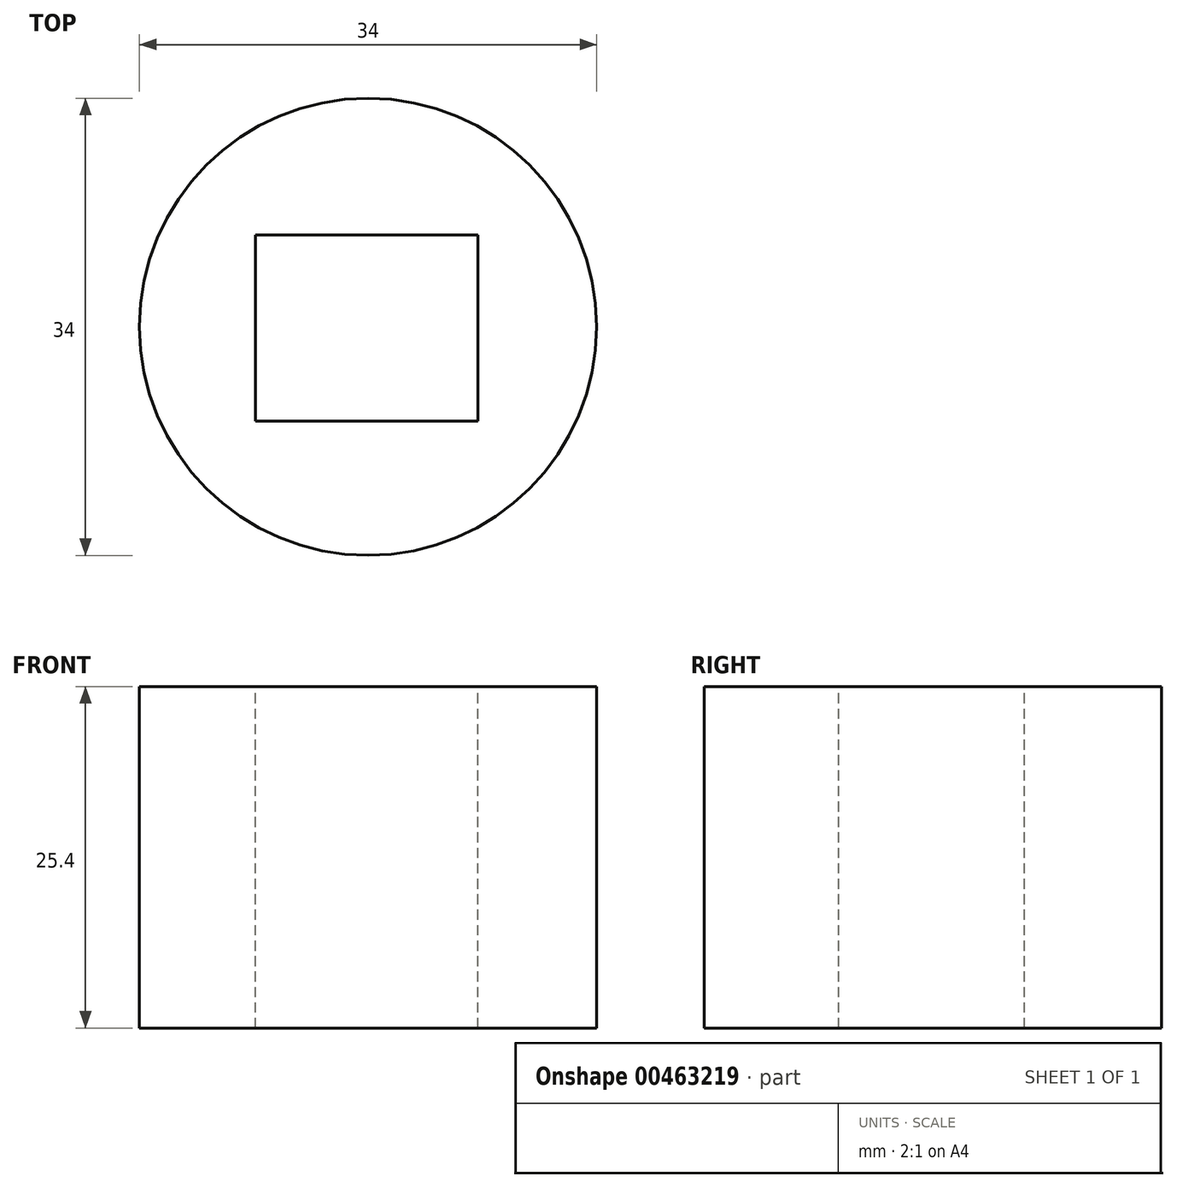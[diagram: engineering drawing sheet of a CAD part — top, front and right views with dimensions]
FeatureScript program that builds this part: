
annotation { "Feature Type Name" : "Feature", "Feature Type Description" : "" }
export const myFeature = defineFeature(function(context is Context, id is Id, definition is map)
    precondition{}
    {
        {
            var Q0;
            Q0=qCreatedBy(makeId("Top.planeOp"),FACE);
            var sketch = newSketch(context, id + "F0", { "sketchPlane" : qUnion([Q0])});
            skCircle(sketch, "E0", {"center": v(0, 0) * mm, "radius": 17 * mm});
            skSolve(sketch);
        }
        {
            var Q0;
            Q0 = qSketchRegion(id + "F0", true);
            extrude(context, id + "F1", {"entities" : qUnion([Q0]), "oppositeDirection" : true, "depth" : 25.4 * mm});
        }
        {
            var Q0;
            Q0=makeQuery(id+"F1.opExtrude","CAP_FACE",FACE,{"disambiguationData":[OSD([sQuery(id+"F0.wireOp",EDGE,"E0")])],"isStart":true});
            var sketch = newSketch(context, id + "F2", { "sketchPlane" : qUnion([Q0])});
            skLineSegment(sketch, "E1.bottom", {"start": v(-8.37, 6.81) * mm, "end": v(8.18, 6.81) * mm});
            skLineSegment(sketch, "E1.top", {"start": v(-8.37, -7) * mm, "end": v(8.18, -7) * mm});
            skLineSegment(sketch, "E1.left", {"start": v(-8.37, 6.81) * mm, "end": v(-8.37, -7) * mm});
            skLineSegment(sketch, "E1.right", {"start": v(8.18, 6.81) * mm, "end": v(8.18, -7) * mm});
            skSolve(sketch);
        }
        {
            var Q0;
            Q0=makeQuery(id+"F2.imprint","IMPRINT",FACE,{"disambiguationData":[TD([[makeQuery(id+"F2.imprint","IMPRINT",EDGE,{"derivedFrom":sQuery(id+"F2.wireOp",EDGE,"E1.bottom")}),-1.0]])]});
            extrude(context, id + "F3", {"entities" : qUnion([Q0]), "operationType" : NewBodyOperationType.REMOVE, "endBound" : BoundingType.THROUGH_ALL, "oppositeDirection" : true, "depth" : 25.4 * mm});
        }
    });
